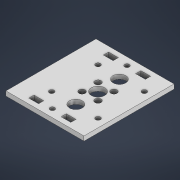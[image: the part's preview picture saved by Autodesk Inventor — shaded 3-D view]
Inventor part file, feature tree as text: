
AUTODESK INVENTOR PART (.ipt)
format: ipt  version: 2022 (Build 260153000, 153)  size: 194,048 bytes
history: native  units: mm
features: extrude x7, sketch x7, pattern_circular x1
ambient origin geometry x8: Origin, YZ Plane, XZ Plane, XY Plane, X Axis, Y Axis, Z Axis, Center Point
bodies: Solid1 (feature_tree)
feature tree (15):
  extrude  "Extrusion1"  Depth=60.0mm
  extrude  "Extrusion2"  Depth=11.8mm
  extrude  "Extrusion3"  Depth=6.5mm
  extrude  "Extrusion4"  Depth=15.0mm
  extrude  "Extrusion5"  Depth=3.5mm
  pattern_circular  "Circular Pattern1"  [2 undecoded]
  extrude  "Extrusion6"  Depth=3.0mm
  extrude  "Extrusion7"  Depth=3.0mm TaperAngle=0.0deg
  sketch  "Sketch1"  dims[d0=52.0mm d1=60.0mm]
  sketch  "Sketch2"  dims[d2=3.0mm d3=0.0mm d4=11.8mm]
  sketch  "Sketch3"  dims[d5=3.4mm d6=6.5mm]
  sketch  "Sketch4"  dims[d7=3.5mm d8=15.0mm]
  sketch  "Sketch5"  dims[d9=6.5mm d10=3.5mm]
  sketch  "Sketch6"  dims[d11=3.0mm d12=0.0mm]
  sketch  "Sketch7"  dims[d13=31.1mm d14=15.5mm d15=8.5mm d16=3.0mm d17=0.0mm d18=10.5mm d19=9.0mm d20=3.0mm d21=0.0mm d22=7.5mm d23=135.0deg d24=4.1mm d25=3.0mm d26=0.0mm d27=40.0mm d28=360.0deg d30=21.85mm d31=45.0deg d32=3.2mm d33=3.2mm d34=0.0mm d35=21.85mm d36=21.85mm d37=21.85mm d38=3.2mm d39=3.2mm d40=3.2mm d41=7.5mm d42=50.0mm d43=3.1mm d44=3.1mm d45=0.0mm]
note: 2 required parameter values undecoded (feature->parameter linkage not recoverable at this tier; creation-order binding heuristic only, values carry confidence <= 0.55)
